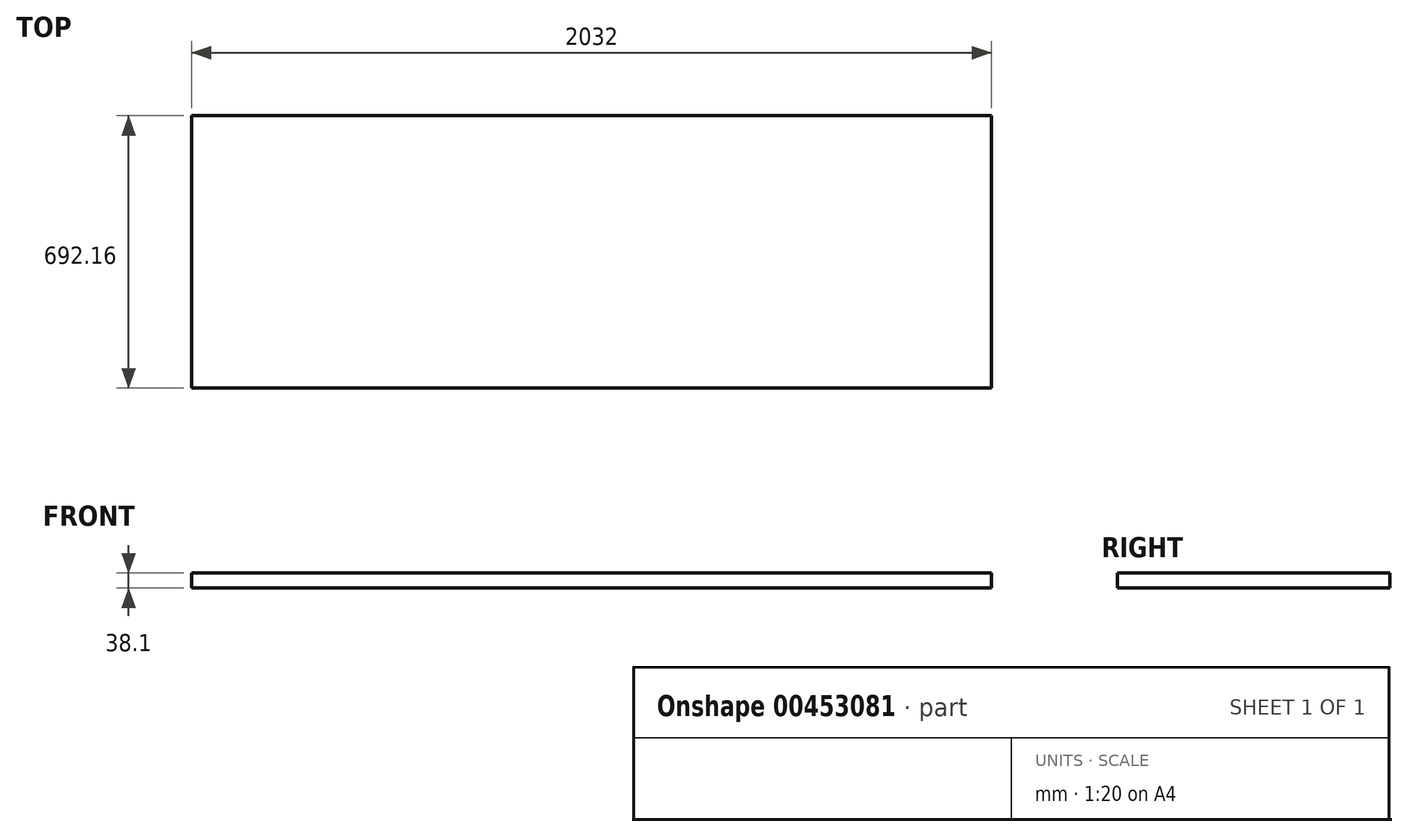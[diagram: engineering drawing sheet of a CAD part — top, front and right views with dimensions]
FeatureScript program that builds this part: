
annotation { "Feature Type Name" : "Feature", "Feature Type Description" : "" }
export const myFeature = defineFeature(function(context is Context, id is Id, definition is map)
    precondition{}
    {
        {
            var Q0;
            Q0=qCreatedBy(makeId("Top.planeOp"),FACE);
            var sketch = newSketch(context, id + "F0", { "sketchPlane" : qUnion([Q0])});
            skLineSegment(sketch, "E0.bottom", {"start": v(1016, 346.07) * mm, "end": v(-1016, 346.07) * mm});
            skLineSegment(sketch, "E0.top", {"start": v(1016, -346.08) * mm, "end": v(-1016, -346.08) * mm});
            skLineSegment(sketch, "E0.left", {"start": v(1016, 346.07) * mm, "end": v(1016, -346.08) * mm});
            skLineSegment(sketch, "E0.right", {"start": v(-1016, 346.08) * mm, "end": v(-1016, -346.08) * mm});
            skPoint(sketch, "E0.middle", {"position": v(0, 0) * mm});
            skSolve(sketch);
        }
        {
            var Q0;
            Q0 = qSketchRegion(id + "F0", true);
            extrude(context, id + "F1", {"entities" : qUnion([Q0]), "depth" : 38.1 * mm, "offsetDistance" : 25.4 * mm});
        }
    });
